# Revit family: Hager-Orion_Plus-IP66-D250-Cl.II-Poly_encl-630A-BE-en
name_source: partatom
category: Electrical Equipment
units: mm (PartAtom-declared; Revit-internal decimal feet)

## family parameters
Cut with Voids When Loaded = No
Host = Face
Panel Configuration = Two Columns, Circuits Across
Part Type = Panelboard
Room Calculation Point = No
Round Connector Dimension = Use Diameter
Shared = No

## types (2) — shared parameters
EF000003 - Mounting method = EV000384 - Surface mounted (plaster)
EF000007 - Colour = EV000270 - Grey
EF000008 - Width = 500 mm  [stored 1.64042 ft]
EF000040 - Height = 650 mm  [stored 2.13255 ft]
EF000049 - Depth = 250 mm  [stored 0.82021 ft]
EF000116 - RAL-number = 7035
EF000118 - With mounting plate = No
EF000266 - Number of rows = 4
EF000339 - Type of cover = EV004216 - Door
EF001088 - Extension possible = No
EF001131 - Internal depth = 250 mm  [stored 0.82021 ft]
EF001596 - Material housing = EV000139 - Plastic
EF002950 - Width in number of modular spacings = 24
EF003532 - Suitable for outdoor use = Yes
EF004427 - Number of modules = 96
EF004464 - Type of door = EV002646 - Single
EF005474 - Degree of protection (IP) = EV006422 - IP66
EF006306 - With lock = Yes
EF007800 - Suitable for lightning protection = No
EF008873 - Nominal current (In) = 630 A
EF009212 - Cover model = EV000116 - Closed
EF015940 - Cover with overpressure release = No
HG000002 - With door or cover = Yes
HG000003 - Range = Orion Plus
HG000006 - Flush mounted = No
HG000009 - Double swing door = No
HG000010 - Asymmetric doors = No
HG000023 - Double section enclosure = No
HG000024 - Bottom section height = 800 mm
HG000026 - Floor standing = No
Manufacturer = Hager
Type Comments = Orion Plus
zero-valued in all types: Default Elevation, EF000218 - Built-in depth, EF000437 - Number of conduit inlets, EF009554 - Number of openings for flange plates, HG000027 - Plinth height

## per-type parameters (varying)
| type | EF004293 - Impact strength | EF006244 - Transparent cover/door | EF009170 - Material plate thickness cabinet | EF009171 - Material plate thickness door/cover | HG000004 - Manufacturer reference |
| Surface mounted (plaster) IP66 W500 H650 D250  - FL221B | EV008784 - IK10 | No | 2 mm  [stored 0.00656168 ft] | 2 mm  [stored 0.00656168 ft] | FL221B |
| Surface mounted (plaster) IP66 W500 H650 D250  - FL271B | EV006814 - IK08 | Yes | 3 mm  [stored 0.00984252 ft] | 3 mm  [stored 0.00984252 ft] | FL271B |

note: [stored X ft] marks values corroborated as IEEE doubles in the binary element streams (Revit-internal decimal feet)

## geometry (parser evidence)
native form markers: Sweep x10
no freeform markers — native parametric forms only
